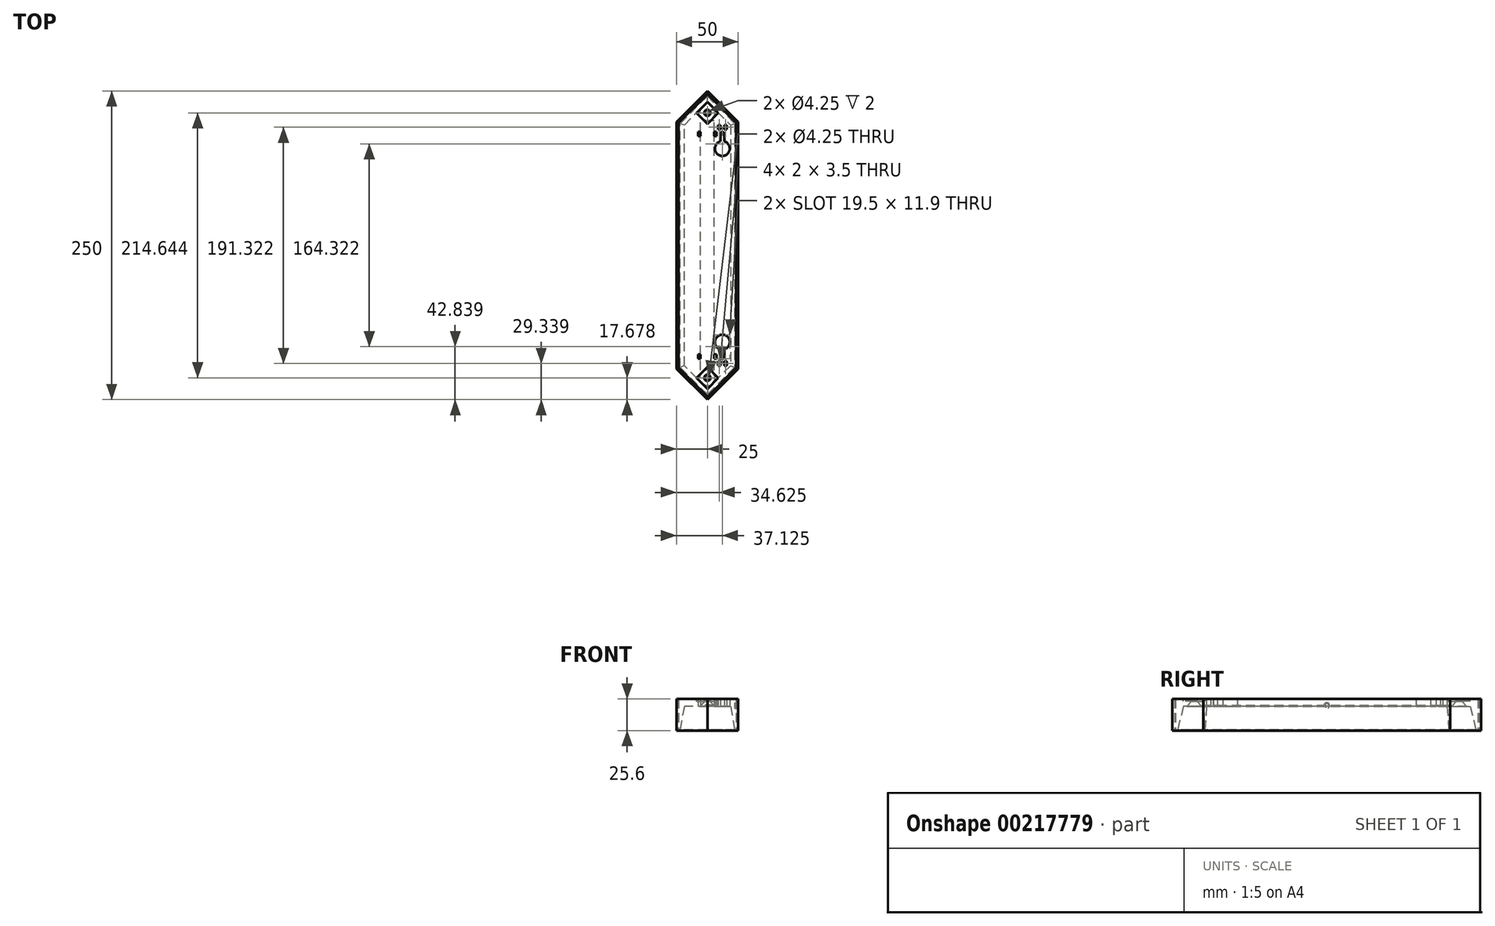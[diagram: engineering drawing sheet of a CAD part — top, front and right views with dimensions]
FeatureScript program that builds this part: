
annotation { "Feature Type Name" : "Feature", "Feature Type Description" : "" }
export const myFeature = defineFeature(function(context is Context, id is Id, definition is map)
    precondition{}
    {
        {
            var Q0;
            Q0=qCreatedBy(makeId("Top.planeOp"),FACE);
            var sketch = newSketch(context, id + "F0", { "sketchPlane" : qUnion([Q0])});
            skLineSegment(sketch, "E0", {"start": v(0, 125) * mm, "end": v(-25, 100) * mm});
            skLineSegment(sketch, "E1", {"start": v(-25, 100) * mm, "end": v(-25, -100) * mm});
            skLineSegment(sketch, "E2", {"start": v(-25, -100) * mm, "end": v(0, -125) * mm});
            skLineSegment(sketch, "E3", {"start": v(0, -125) * mm, "end": v(25, -100) * mm});
            skLineSegment(sketch, "E4", {"start": v(25, -100) * mm, "end": v(25, 100) * mm});
            skLineSegment(sketch, "E5", {"start": v(25, 100) * mm, "end": v(0, 125) * mm});
            skLineSegment(sketch, "E6.0", {"start": v(23.8, -99.5) * mm, "end": v(23.8, 99.5) * mm});
            skLineSegment(sketch, "E6.1", {"start": v(0, 123.3) * mm, "end": v(-23.8, 99.5) * mm});
            skLineSegment(sketch, "E6.2", {"start": v(-23.8, 99.5) * mm, "end": v(-23.8, -99.5) * mm});
            skLineSegment(sketch, "E6.3", {"start": v(23.8, 99.5) * mm, "end": v(0, 123.3) * mm});
            skLineSegment(sketch, "E6.4", {"start": v(-23.8, -99.5) * mm, "end": v(0, -123.3) * mm});
            skLineSegment(sketch, "E6.5", {"start": v(0, -123.3) * mm, "end": v(23.8, -99.5) * mm});
            skSolve(sketch);
        }
        {
            var Q0;
            Q0 = qSketchRegion(id + "F0", true);
            var Q1;
            Q1=makeQuery(id+"F0.imprint","IMPRINT",FACE,{"disambiguationData":[TD([[makeQuery(id+"F0.imprint","IMPRINT",EDGE,{"derivedFrom":sQuery(id+"F0.wireOp",EDGE,"E6.0")}),1.0]])]});
            extrude(context, id + "F1", {"entities" : qUnion([Q0, Q1]), "oppositeDirection" : true, "depth" : 0.6 * mm});
        }
        {
            var Q0;
            Q0 = qSketchRegion(id + "F0", true);
            extrude(context, id + "F2", {"entities" : qUnion([Q0]), "operationType" : NewBodyOperationType.ADD, "depth" : 25 * mm});
        }
        {
            var Q0;
            Q0=qCreatedBy(makeId("Front.planeOp"),FACE);
            var sketch = newSketch(context, id + "F3", { "sketchPlane" : qUnion([Q0])});
            skLineSegment(sketch, "E7.0", {"start": v(23.8, 19.76) * mm, "end": v(23.8, 17.53) * mm});
            skArc(sketch, "E8", {"start": v(22.8, 19.76) * mm, "mid": v(23.06, 18.54) * mm, "end": v(23.8, 17.53) * mm});
            skLineSegment(sketch, "E9", {"start": v(23.8, 19.76) * mm, "end": v(25.8, 19.76) * mm, "construction": true});
            skPoint(sketch, "E10", {"position": v(22.8, 19.76) * mm});
            skPoint(sketch, "E11.orphan", {"position": v(23.8, 25) * mm});
            skPoint(sketch, "E12.orphan", {"position": v(23.8, 0) * mm});
            skLineSegment(sketch, "E13", {"start": v(23.8, 19.76) * mm, "end": v(22.8, 19.76) * mm});
            skPoint(sketch, "E14", {"position": v(23.8, 22) * mm});
            skSolve(sketch);
        }
        {
            var Q0;
            Q0=makeQuery(id+"F3.imprint","IMPRINT",FACE,{"disambiguationData":[TD([[makeQuery(id+"F3.imprint","IMPRINT",EDGE,{"derivedFrom":sQuery(id+"F3.wireOp",EDGE,"E7.0")}),-1.0]])]});
            var Q1;
            Q1=sQuery(id+"F3.wireOp",EDGE,"E13");
            revolve(context, id + "F4", {"operationType" : NewBodyOperationType.ADD, "entities" : qUnion([Q0]), "axis" : qUnion([Q1]), "revolveType" : RevolveType.FULL});
        }
        {
            var Q0;
            Q0=makeQuery(id+"F1.opExtrude","CAP_FACE",FACE,{"disambiguationData":[OSD([sQuery(id+"F0.wireOp",EDGE,"E0"),sQuery(id+"F0.wireOp",EDGE,"E1"),sQuery(id+"F0.wireOp",EDGE,"E2"),sQuery(id+"F0.wireOp",EDGE,"E3"),sQuery(id+"F0.wireOp",EDGE,"E4"),sQuery(id+"F0.wireOp",EDGE,"E5")])],"isStart":true});
            var sketch = newSketch(context, id + "F5", { "sketchPlane" : qUnion([Q0])});
            skLineSegment(sketch, "E15.0", {"start": v(0, 122.6) * mm, "end": v(-23.3, 99.3) * mm});
            skLineSegment(sketch, "E15.1", {"start": v(-23.3, -99.3) * mm, "end": v(0, -122.6) * mm});
            skLineSegment(sketch, "E15.2", {"start": v(0, -122.6) * mm, "end": v(23.3, -99.3) * mm});
            skLineSegment(sketch, "E15.3", {"start": v(-23.3, 99.3) * mm, "end": v(-23.3, -99.3) * mm});
            skLineSegment(sketch, "E15.4", {"start": v(23.3, -99.3) * mm, "end": v(23.3, 99.3) * mm});
            skLineSegment(sketch, "E15.5", {"start": v(23.3, 99.3) * mm, "end": v(0, 122.6) * mm});
            skSolve(sketch);
        }
        {
            var Q0;
            Q0 = qSketchRegion(id + "F5", true);
            var Q1;
            Q1=makeQuery(id+"F2.opExtrude","CAP_FACE",FACE,{"disambiguationData":[OSD([sQuery(id+"F0.wireOp",EDGE,"E0"),sQuery(id+"F0.wireOp",EDGE,"E1"),sQuery(id+"F0.wireOp",EDGE,"E2"),sQuery(id+"F0.wireOp",EDGE,"E3"),sQuery(id+"F0.wireOp",EDGE,"E4"),sQuery(id+"F0.wireOp",EDGE,"E5"),sQuery(id+"F0.wireOp",EDGE,"E6.0"),sQuery(id+"F0.wireOp",EDGE,"E6.1"),sQuery(id+"F0.wireOp",EDGE,"E6.2"),sQuery(id+"F0.wireOp",EDGE,"E6.3"),sQuery(id+"F0.wireOp",EDGE,"E6.4"),sQuery(id+"F0.wireOp",EDGE,"E6.5")])],"isStart":false});
            extrude(context, id + "F6", {"entities" : qUnion([Q0]), "endBound" : BoundingType.UP_TO_SURFACE, "endBoundEntityFace" : qUnion([Q1]), "depth" : 25 * mm});
        }
        {
            var Q0;
            Q0=makeQuery(id+"F6.opExtrude","SWEPT_FACE",FACE,{"disambiguationData":[OSD([sQuery(id+"F5.wireOp",EDGE,"E15.4")])]});
            var sketch = newSketch(context, id + "F7", { "sketchPlane" : qUnion([Q0])});
            skCircle(sketch, "E16.0", {"center": v(0, 19.76) * mm, "radius": 2.24 * mm});
            skSolve(sketch);
        }
        {
            var Q0;
            Q0 = qSketchRegion(id + "F7", true);
            extrude(context, id + "F8", {"entities" : qUnion([Q0]), "operationType" : NewBodyOperationType.REMOVE, "oppositeDirection" : true, "depth" : 1 * mm});
        }
        {
            var Q0;
            Q0=makeQuery(id+"F6.opExtrude","CAP_FACE",FACE,{"disambiguationData":[OSD([sQuery(id+"F5.wireOp",EDGE,"E15.0"),sQuery(id+"F5.wireOp",EDGE,"E15.1"),sQuery(id+"F5.wireOp",EDGE,"E15.2"),sQuery(id+"F5.wireOp",EDGE,"E15.3"),sQuery(id+"F5.wireOp",EDGE,"E15.4"),sQuery(id+"F5.wireOp",EDGE,"E15.5")])],"isStart":true});
            var sketch = newSketch(context, id + "F9", { "sketchPlane" : qUnion([Q0])});
            skLineSegment(sketch, "E17.0", {"start": v(22.1, -98.8) * mm, "end": v(22.1, 98.8) * mm});
            skLineSegment(sketch, "E17.1", {"start": v(0, 120.9) * mm, "end": v(-22.1, 98.8) * mm});
            skLineSegment(sketch, "E17.2", {"start": v(-22.1, 98.8) * mm, "end": v(-22.1, -98.8) * mm});
            skLineSegment(sketch, "E17.3", {"start": v(22.1, 98.8) * mm, "end": v(0, 120.9) * mm});
            skLineSegment(sketch, "E17.4", {"start": v(-22.1, -98.8) * mm, "end": v(0, -120.9) * mm});
            skLineSegment(sketch, "E17.5", {"start": v(0, -120.9) * mm, "end": v(22.1, -98.8) * mm});
            skSolve(sketch);
        }
        {
            var Q0;
            Q0 = qSketchRegion(id + "F9", true);
            var Q1;
            Q1=qCreatedBy(id+"FNFugZNVum9jf9h_2.planeOp",FACE);
            extrude(context, id + "F10", {"entities" : qUnion([Q0]), "operationType" : NewBodyOperationType.REMOVE, "oppositeDirection" : true, "endBoundEntityFace" : qUnion([Q1]), "depth" : 19 * mm, "hasDraft" : true, "draftAngle" : 10 * degree, "draftPullDirection" : true});
        }
        {
            var Q0;
            Q0=makeQuery(id+"F6.opExtrude","CAP_FACE",FACE,{"disambiguationData":[OSD([sQuery(id+"F5.wireOp",EDGE,"E15.0"),sQuery(id+"F5.wireOp",EDGE,"E15.1"),sQuery(id+"F5.wireOp",EDGE,"E15.2"),sQuery(id+"F5.wireOp",EDGE,"E15.3"),sQuery(id+"F5.wireOp",EDGE,"E15.4"),sQuery(id+"F5.wireOp",EDGE,"E15.5")])],"isStart":false});
            var sketch = newSketch(context, id + "F11", { "sketchPlane" : qUnion([Q0])});
            skPoint(sketch, "E18.middle", {"position": v(0, 107.32) * mm});
            skCircle(sketch, "E19", {"center": v(0, -107.32) * mm, "radius": 2.52 * mm});
            skCircle(sketch, "E20", {"center": v(0, 107.32) * mm, "radius": 2.52 * mm});
            skLineSegment(sketch, "E21.0", {"start": v(-18.75, 97.41) * mm, "end": v(0, 116.16) * mm, "construction": true});
            skLineSegment(sketch, "E22.0", {"start": v(0, 116.16) * mm, "end": v(18.75, 97.41) * mm, "construction": true});
            skLineSegment(sketch, "E23.0", {"start": v(18.75, -97.41) * mm, "end": v(0, -116.16) * mm, "construction": true});
            skLineSegment(sketch, "E24.0", {"start": v(0, -116.16) * mm, "end": v(-18.75, -97.41) * mm, "construction": true});
            skLineSegment(sketch, "E25", {"start": v(0, 116.16) * mm, "end": v(8.84, 107.32) * mm});
            skLineSegment(sketch, "E26", {"start": v(8.84, 107.32) * mm, "end": v(0, 98.48) * mm});
            skLineSegment(sketch, "E27", {"start": v(0, 98.48) * mm, "end": v(-8.84, 107.32) * mm});
            skLineSegment(sketch, "E28", {"start": v(-8.84, 107.32) * mm, "end": v(0, 116.16) * mm});
            skLineSegment(sketch, "E29", {"start": v(0, -116.16) * mm, "end": v(8.84, -107.32) * mm});
            skLineSegment(sketch, "E30", {"start": v(8.84, -107.32) * mm, "end": v(0, -98.48) * mm});
            skLineSegment(sketch, "E31", {"start": v(0, -98.48) * mm, "end": v(-8.84, -107.32) * mm});
            skLineSegment(sketch, "E32", {"start": v(-8.84, -107.32) * mm, "end": v(0, -116.16) * mm});
            skSolve(sketch);
        }
        {
            var Q0;
            Q0 = qSketchRegion(id + "F11", true);
            extrude(context, id + "F12", {"entities" : qUnion([Q0]), "operationType" : NewBodyOperationType.REMOVE, "oppositeDirection" : true, "depth" : 2 * mm});
        }
        {
            var Q0;
            {var subQ0=sQuery(id+"F5.wireOp",EDGE,"E15.5");var subQ1=sQuery(id+"F5.wireOp",EDGE,"E15.4");var subQ2=sQuery(id+"F5.wireOp",EDGE,"E15.0");var subQ3=sQuery(id+"F5.wireOp",EDGE,"E15.3");var subQ4=sQuery(id+"F5.wireOp",EDGE,"E15.1");var subQ5=sQuery(id+"F5.wireOp",EDGE,"E15.2");Q0=makeQuery(id+"F12.boolean.opBoolean","SPLIT",FACE,{"disambiguationData":[TD([makeQuery(id+"F6.opExtrude","SWEPT_FACE",FACE,{"disambiguationData":[OSD([subQ2])]})])],"derivedFrom":makeQuery(id+"F6.opExtrude","CAP_FACE",FACE,{"disambiguationData":[OSD([subQ2,subQ4,subQ5,subQ3,subQ1,subQ0])],"isStart":false})});}
            var sketch = newSketch(context, id + "F13", { "sketchPlane" : qUnion([Q0])});
            skCircle(sketch, "E33", {"center": v(0, -107.32) * mm, "radius": 2.12 * mm});
            skCircle(sketch, "E34", {"center": v(0, 107.32) * mm, "radius": 2.12 * mm});
            skSolve(sketch);
        }
        {
            var Q0;
            Q0 = qSketchRegion(id + "F13", true);
            extrude(context, id + "F14", {"entities" : qUnion([Q0]), "operationType" : NewBodyOperationType.REMOVE, "endBound" : BoundingType.THROUGH_ALL, "oppositeDirection" : true, "depth" : 25 * mm, "hasSecondDirection" : true, "secondDirectionBound" : SecondDirectionBoundingType.THROUGH_ALL, "secondDirectionOppositeDirection" : false, "secondDirectionDepth" : 25 * mm});
        }
        {
            var Q0;
            Q0=makeQuery(id+"F14.boolean.opBoolean","INTERSECT",EDGE,{"derivedFrom":[makeQuery(id+"F10.boolean.opBoolean","COPY",FACE,{"derivedFrom":makeQuery(id+"F10.opExtrude","CAP_FACE",FACE,{"disambiguationData":[OSD([sQuery(id+"F9.wireOp",EDGE,"E17.0"),sQuery(id+"F9.wireOp",EDGE,"E17.1"),sQuery(id+"F9.wireOp",EDGE,"E17.2"),sQuery(id+"F9.wireOp",EDGE,"E17.3"),sQuery(id+"F9.wireOp",EDGE,"E17.4"),sQuery(id+"F9.wireOp",EDGE,"E17.5")])],"isStart":false})}),makeQuery(id+"F14.opExtrude","SWEPT_FACE",FACE,{"disambiguationData":[OSD([sQuery(id+"F13.wireOp",EDGE,"E33")])]})]});
            var Q1;
            Q1=makeQuery(id+"F14.boolean.opBoolean","INTERSECT",EDGE,{"derivedFrom":[makeQuery(id+"F10.boolean.opBoolean","COPY",FACE,{"derivedFrom":makeQuery(id+"F10.opExtrude","CAP_FACE",FACE,{"disambiguationData":[OSD([sQuery(id+"F9.wireOp",EDGE,"E17.0"),sQuery(id+"F9.wireOp",EDGE,"E17.1"),sQuery(id+"F9.wireOp",EDGE,"E17.2"),sQuery(id+"F9.wireOp",EDGE,"E17.3"),sQuery(id+"F9.wireOp",EDGE,"E17.4"),sQuery(id+"F9.wireOp",EDGE,"E17.5")])],"isStart":false})}),makeQuery(id+"F14.opExtrude","SWEPT_FACE",FACE,{"disambiguationData":[OSD([sQuery(id+"F13.wireOp",EDGE,"E34")])]})]});
            chamfer(context, id + "F15", {"entities" : qUnion([Q0, Q1]), "width" : 4 * mm, "tangentPropagation" : true});
        }
        {
            var Q0;
            Q0=makeQuery(id+"F10.boolean.opBoolean","COPY",FACE,{"derivedFrom":makeQuery(id+"F10.opExtrude","CAP_FACE",FACE,{"disambiguationData":[OSD([sQuery(id+"F9.wireOp",EDGE,"E17.0"),sQuery(id+"F9.wireOp",EDGE,"E17.1"),sQuery(id+"F9.wireOp",EDGE,"E17.2"),sQuery(id+"F9.wireOp",EDGE,"E17.3"),sQuery(id+"F9.wireOp",EDGE,"E17.4"),sQuery(id+"F9.wireOp",EDGE,"E17.5")])],"isStart":false})});
            var sketch = newSketch(context, id + "F16", { "sketchPlane" : qUnion([Q0])});
            skLineSegment(sketch, "E35.bottom", {"start": v(5.5, 101) * mm, "end": v(-5.5, 101) * mm});
            skLineSegment(sketch, "E35.top", {"start": v(5.5, -101) * mm, "end": v(-5.5, -101) * mm});
            skLineSegment(sketch, "E35.left", {"start": v(5.5, 101) * mm, "end": v(5.5, -101) * mm});
            skLineSegment(sketch, "E35.right", {"start": v(-5.5, 101) * mm, "end": v(-5.5, -101) * mm});
            skPoint(sketch, "E35.middle", {"position": v(0, 0) * mm});
            skSolve(sketch);
        }
        {
            var Q0;
            Q0 = qSketchRegion(id + "F16", true);
            extrude(context, id + "F17", {"entities" : qUnion([Q0]), "operationType" : NewBodyOperationType.REMOVE, "oppositeDirection" : true, "depth" : 1 * mm});
        }
        {
            var Q0;
            Q0=makeQuery(id+"F10.boolean.opBoolean","COPY",FACE,{"derivedFrom":makeQuery(id+"F10.opExtrude","CAP_FACE",FACE,{"disambiguationData":[OSD([sQuery(id+"F9.wireOp",EDGE,"E17.0"),sQuery(id+"F9.wireOp",EDGE,"E17.1"),sQuery(id+"F9.wireOp",EDGE,"E17.2"),sQuery(id+"F9.wireOp",EDGE,"E17.3"),sQuery(id+"F9.wireOp",EDGE,"E17.4"),sQuery(id+"F9.wireOp",EDGE,"E17.5")])],"isStart":false})});
            var sketch = newSketch(context, id + "F18", { "sketchPlane" : qUnion([Q0])});
            skLineSegment(sketch, "E36.bottom", {"start": v(-5.5, -92) * mm, "end": v(-7.5, -92) * mm});
            skLineSegment(sketch, "E36.top", {"start": v(-5.5, -88.5) * mm, "end": v(-7.5, -88.5) * mm});
            skLineSegment(sketch, "E36.left", {"start": v(-5.5, -92) * mm, "end": v(-5.5, -88.5) * mm});
            skLineSegment(sketch, "E36.right", {"start": v(-7.5, -92) * mm, "end": v(-7.5, -88.5) * mm});
            skLineSegment(sketch, "E37.bottom", {"start": v(5.5, -92) * mm, "end": v(7.5, -92) * mm});
            skLineSegment(sketch, "E37.top", {"start": v(5.5, -88.5) * mm, "end": v(7.5, -88.5) * mm});
            skLineSegment(sketch, "E37.left", {"start": v(5.5, -92) * mm, "end": v(5.5, -88.5) * mm});
            skLineSegment(sketch, "E37.right", {"start": v(7.5, -92) * mm, "end": v(7.5, -88.5) * mm});
            skLineSegment(sketch, "E38.bottom", {"start": v(-5.5, 92) * mm, "end": v(-7.5, 92) * mm});
            skLineSegment(sketch, "E38.top", {"start": v(-5.5, 88.5) * mm, "end": v(-7.5, 88.5) * mm});
            skLineSegment(sketch, "E38.left", {"start": v(-5.5, 92) * mm, "end": v(-5.5, 88.5) * mm});
            skLineSegment(sketch, "E38.right", {"start": v(-7.5, 92) * mm, "end": v(-7.5, 88.5) * mm});
            skLineSegment(sketch, "E39.bottom", {"start": v(5.5, 92) * mm, "end": v(7.5, 92) * mm});
            skLineSegment(sketch, "E39.top", {"start": v(5.5, 88.5) * mm, "end": v(7.5, 88.5) * mm});
            skLineSegment(sketch, "E39.left", {"start": v(5.5, 92) * mm, "end": v(5.5, 88.5) * mm});
            skLineSegment(sketch, "E39.right", {"start": v(7.5, 92) * mm, "end": v(7.5, 88.5) * mm});
            skArc(sketch, "E40", {"start": v(13.62, 84.22) * mm, "mid": v(12.12, 72.41) * mm, "end": v(10.62, 84.22) * mm});
            skArc(sketch, "E41", {"start": v(13.62, 90.41) * mm, "mid": v(12.12, 91.91) * mm, "end": v(10.62, 90.41) * mm});
            skLineSegment(sketch, "E42", {"start": v(12.12, 90.41) * mm, "end": v(12.12, 78.41) * mm, "construction": true});
            skLineSegment(sketch, "E43", {"start": v(10.62, 84.22) * mm, "end": v(10.62, 90.41) * mm});
            skLineSegment(sketch, "E44", {"start": v(13.62, 90.41) * mm, "end": v(13.62, 84.22) * mm});
            skLineSegment(sketch, "E45.bottom", {"start": v(8.62, 97.41) * mm, "end": v(10.62, 97.41) * mm});
            skLineSegment(sketch, "E45.top", {"start": v(8.62, 93.91) * mm, "end": v(10.62, 93.91) * mm});
            skLineSegment(sketch, "E45.left", {"start": v(8.62, 97.41) * mm, "end": v(8.62, 93.91) * mm});
            skLineSegment(sketch, "E45.right", {"start": v(10.62, 97.41) * mm, "end": v(10.62, 93.91) * mm});
            skLineSegment(sketch, "E46.bottom", {"start": v(13.62, 97.41) * mm, "end": v(15.62, 97.41) * mm});
            skLineSegment(sketch, "E46.top", {"start": v(13.62, 93.91) * mm, "end": v(15.62, 93.91) * mm});
            skLineSegment(sketch, "E46.left", {"start": v(13.62, 97.41) * mm, "end": v(13.62, 93.91) * mm});
            skLineSegment(sketch, "E46.right", {"start": v(15.62, 97.41) * mm, "end": v(15.62, 93.91) * mm});
            skPoint(sketch, "E47", {"position": v(12.12, 91.91) * mm});
            skArc(sketch, "E48.MirrorCS", {"start": v(13.62, -84.22) * mm, "mid": v(12.12, -72.41) * mm, "end": v(10.62, -84.22) * mm});
            skLineSegment(sketch, "E49.MirrorCS", {"start": v(10.62, -84.22) * mm, "end": v(10.62, -90.41) * mm});
            skArc(sketch, "E50.MirrorCS", {"start": v(13.62, -90.41) * mm, "mid": v(12.12, -91.91) * mm, "end": v(10.62, -90.41) * mm});
            skLineSegment(sketch, "E51.MirrorCS", {"start": v(13.62, -90.41) * mm, "end": v(13.62, -84.22) * mm});
            skLineSegment(sketch, "E52.MirrorCS", {"start": v(8.62, -97.41) * mm, "end": v(8.62, -93.91) * mm});
            skLineSegment(sketch, "E53.MirrorCS", {"start": v(8.62, -97.41) * mm, "end": v(10.62, -97.41) * mm});
            skLineSegment(sketch, "E54.MirrorCS", {"start": v(10.62, -97.41) * mm, "end": v(10.62, -93.91) * mm});
            skLineSegment(sketch, "E55.MirrorCS", {"start": v(8.62, -93.91) * mm, "end": v(10.62, -93.91) * mm});
            skLineSegment(sketch, "E56.MirrorCS", {"start": v(13.62, -93.91) * mm, "end": v(15.62, -93.91) * mm});
            skLineSegment(sketch, "E57.MirrorCS", {"start": v(13.62, -97.41) * mm, "end": v(13.62, -93.91) * mm});
            skLineSegment(sketch, "E58.MirrorCS", {"start": v(13.62, -97.41) * mm, "end": v(15.62, -97.41) * mm});
            skLineSegment(sketch, "E59.MirrorCS", {"start": v(15.62, -97.41) * mm, "end": v(15.62, -93.91) * mm});
            skSolve(sketch);
        }
        {
            var Q0;
            Q0 = qSketchRegion(id + "F18", true);
            extrude(context, id + "F19", {"entities" : qUnion([Q0]), "operationType" : NewBodyOperationType.REMOVE, "endBound" : BoundingType.THROUGH_ALL, "oppositeDirection" : true, "depth" : 25 * mm});
        }
    });
